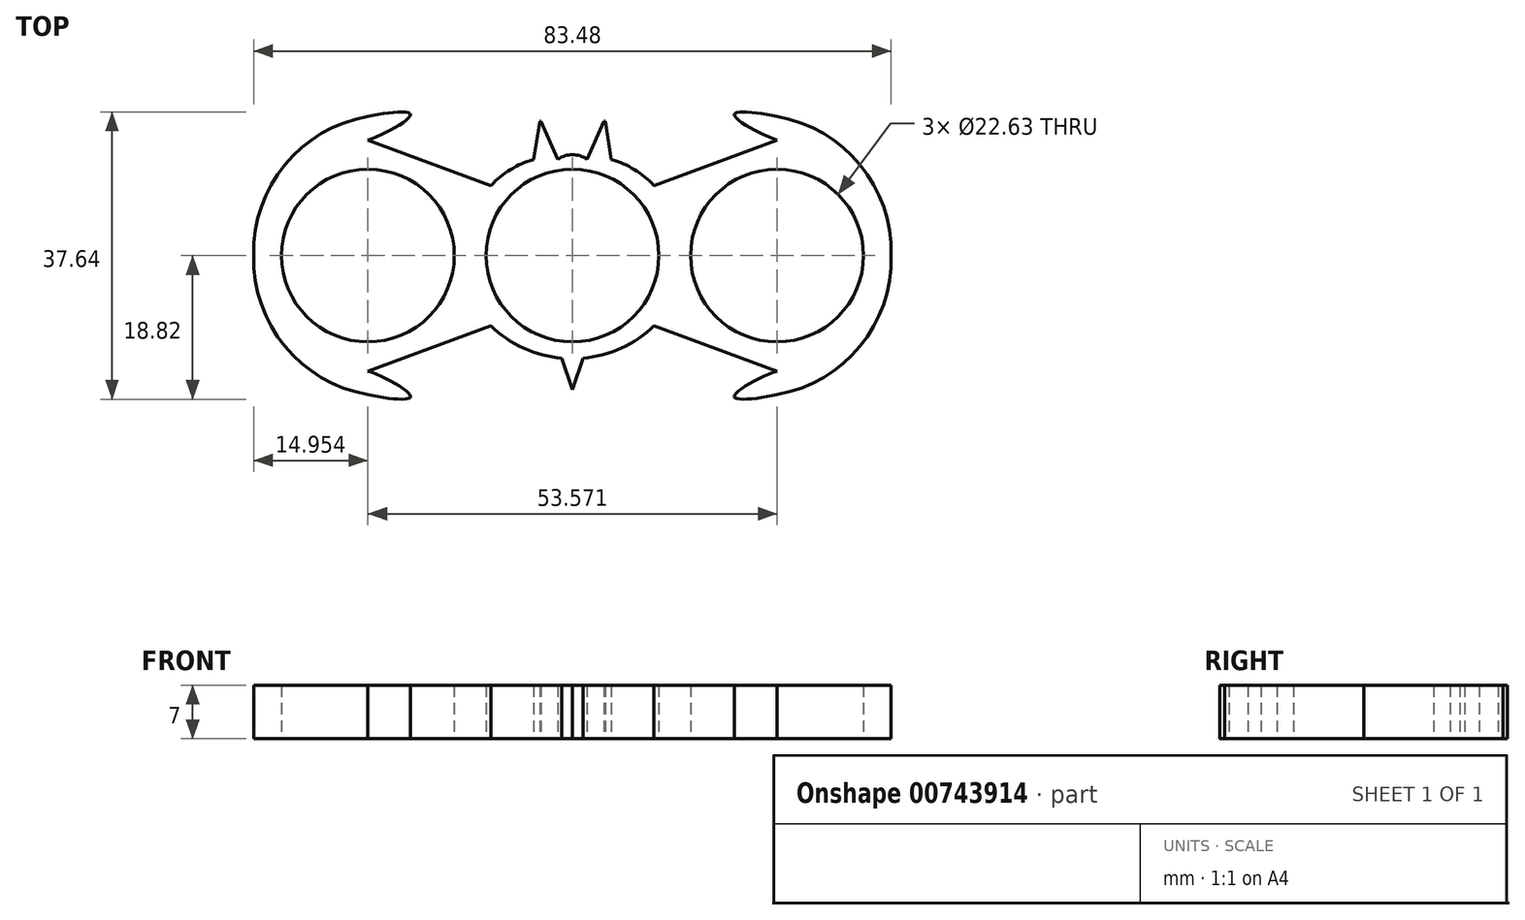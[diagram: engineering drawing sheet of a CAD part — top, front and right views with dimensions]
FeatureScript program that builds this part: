
annotation { "Feature Type Name" : "Feature", "Feature Type Description" : "" }
export const myFeature = defineFeature(function(context is Context, id is Id, definition is map)
    precondition{}
    {
        {
            var Q0;
            Q0=qCreatedBy(makeId("Top.planeOp"),FACE);
            var sketch = newSketch(context, id + "F0", { "sketchPlane" : qUnion([Q0])});
            skCircle(sketch, "E0", {"center": v(0, 0) * mm, "radius": 11.32 * mm});
            skCircle(sketch, "E1", {"center": v(0, 0) * mm, "radius": 45 * mm, "construction": true});
            skLineSegment(sketch, "E2", {"start": v(-5.1, 12.6) * mm, "end": v(-4.3, 17.6) * mm});
            skLineSegment(sketch, "E3", {"start": v(-4.3, 17.6) * mm, "end": v(-4.15, 17.6) * mm});
            skLineSegment(sketch, "E4", {"start": v(-4.15, 17.6) * mm, "end": v(-1.9, 12.6) * mm});
            skArc(sketch, "E5", {"start": v(-5.1, 12.6) * mm, "mid": v(-8.11, 11.26) * mm, "end": v(-10.68, 9.17) * mm});
            skArc(sketch, "E6.MirrorCS", {"start": v(5.1, 12.6) * mm, "mid": v(8.11, 11.26) * mm, "end": v(10.68, 9.17) * mm});
            skLineSegment(sketch, "E7.MirrorCS", {"start": v(5.1, 12.6) * mm, "end": v(4.3, 17.6) * mm});
            skLineSegment(sketch, "E8.MirrorCS", {"start": v(4.15, 17.6) * mm, "end": v(1.9, 12.6) * mm});
            skLineSegment(sketch, "E9.MirrorCS", {"start": v(4.3, 17.6) * mm, "end": v(4.15, 17.6) * mm});
            skArc(sketch, "E10", {"start": v(1.9, 12.6) * mm, "mid": v(0, 13.21) * mm, "end": v(-1.9, 12.6) * mm});
            skArc(sketch, "E11", {"start": v(-10.68, -9.17) * mm, "mid": v(-6.4, -12.14) * mm, "end": v(-1.38, -13.45) * mm});
            skLineSegment(sketch, "E12", {"start": v(-1.38, -13.45) * mm, "end": v(0, -17.6) * mm});
            skArc(sketch, "E13.MirrorCS", {"start": v(10.68, -9.17) * mm, "mid": v(6.4, -12.14) * mm, "end": v(1.38, -13.45) * mm});
            skLineSegment(sketch, "E14.MirrorCS", {"start": v(1.38, -13.45) * mm, "end": v(0, -17.6) * mm});
            skCircle(sketch, "E15", {"center": v(-26.79, 0) * mm, "radius": 11.32 * mm});
            skLineSegment(sketch, "E16", {"start": v(-26.79, 0) * mm, "end": v(-26.79, 26.28) * mm, "construction": true});
            skLineSegment(sketch, "E17", {"start": v(-26.79, 0) * mm, "end": v(-26.79, -29.82) * mm, "construction": true});
            skLineSegment(sketch, "E18", {"start": v(-10.68, 9.17) * mm, "end": v(-26.79, 15.14) * mm});
            skLineSegment(sketch, "E19.MirrorCS", {"start": v(-10.68, -9.17) * mm, "end": v(-26.79, -15.14) * mm});
            skArc(sketch, "E20", {"start": v(-26.79, 18.22) * mm, "mid": v(-37.65, 11.89) * mm, "end": v(-41.73, 0) * mm});
            skArc(sketch, "E21.MirrorCS", {"start": v(-26.79, -18.22) * mm, "mid": v(-37.65, -11.89) * mm, "end": v(-41.73, 0) * mm});
            skFitSpline(sketch, "E22", {"points": [v(-26.79, 18.22) * mm, v(-21.2, 18.46) * mm, v(-26.79, 15.14) * mm], "startDerivative": vector(14.49, 3.26) * mm, "endDerivative": vector(-11.35, -3.52) * mm});
            skFitSpline(sketch, "E23.MirrorCS", {"points": [v(-26.79, -18.22) * mm, v(-21.2, -18.46) * mm, v(-26.79, -15.14) * mm], "startDerivative": vector(14.49, -3.26) * mm, "endDerivative": vector(-11.35, 3.52) * mm});
            skLineSegment(sketch, "E24.MirrorCS", {"start": v(10.68, 9.17) * mm, "end": v(26.79, 15.14) * mm});
            skFitSpline(sketch, "E25.MirrorCS", {"points": [v(26.79, 18.22) * mm, v(21.2, 18.46) * mm, v(26.79, 15.14) * mm], "startDerivative": vector(-14.49, 3.26) * mm, "endDerivative": vector(11.35, -3.52) * mm});
            skArc(sketch, "E26.MirrorCS", {"start": v(26.79, 18.22) * mm, "mid": v(37.65, 11.89) * mm, "end": v(41.73, 0) * mm});
            skArc(sketch, "E27.MirrorCS", {"start": v(26.79, -18.22) * mm, "mid": v(37.65, -11.89) * mm, "end": v(41.73, 0) * mm});
            skFitSpline(sketch, "E28.MirrorCS", {"points": [v(26.79, -18.22) * mm, v(21.2, -18.46) * mm, v(26.79, -15.14) * mm], "startDerivative": vector(-14.49, -3.26) * mm, "endDerivative": vector(11.35, 3.52) * mm});
            skLineSegment(sketch, "E29.MirrorCS", {"start": v(10.68, -9.17) * mm, "end": v(26.79, -15.14) * mm});
            skCircle(sketch, "E30.MirrorC", {"center": v(26.79, 0) * mm, "radius": 11.32 * mm});
            skSolve(sketch);
        }
        {
            var Q0;
            Q0=qSketchRegion(id+"F0",true);
            extrude(context, id + "F1", {"entities" : qUnion([Q0]), "depth" : 7 * mm, "offsetDistance" : 25 * mm});
        }
    });
